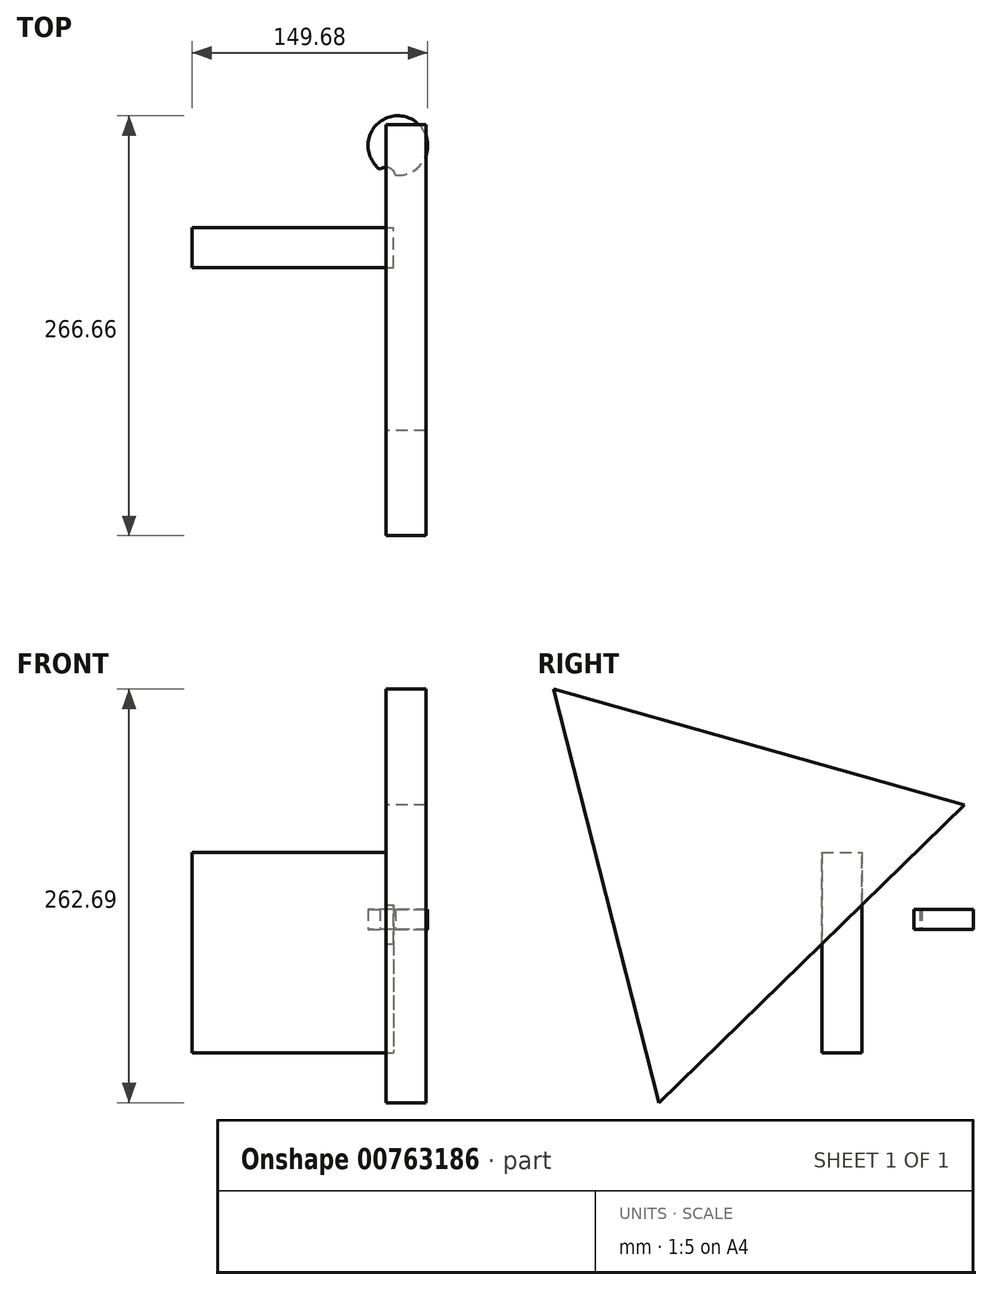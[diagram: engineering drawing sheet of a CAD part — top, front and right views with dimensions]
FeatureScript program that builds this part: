
annotation { "Feature Type Name" : "Feature", "Feature Type Description" : "" }
export const myFeature = defineFeature(function(context is Context, id is Id, definition is map)
    precondition{}
    {
        {
            var Q0;
            Q0=qCreatedBy(makeId("Front.planeOp"),FACE);
            var sketch = newSketch(context, id + "F0", { "sketchPlane" : qUnion([Q0])});
            skLineSegment(sketch, "E0.bottom", {"start": v(-123.14, 48.88) * mm, "end": v(4.73, 48.88) * mm});
            skLineSegment(sketch, "E0.top", {"start": v(-123.14, -78.51) * mm, "end": v(4.73, -78.51) * mm});
            skLineSegment(sketch, "E0.left", {"start": v(-123.14, 48.88) * mm, "end": v(-123.14, -78.51) * mm});
            skLineSegment(sketch, "E0.right", {"start": v(4.73, 48.88) * mm, "end": v(4.73, -78.51) * mm});
            skSolve(sketch);
        }
        {
            var Q0;
            Q0=makeQuery(id+"F0.imprint","IMPRINT",FACE,{"disambiguationData":[TD([[makeQuery(id+"F0.imprint","IMPRINT",EDGE,{"derivedFrom":sQuery(id+"F0.wireOp",EDGE,"E0.bottom")}),-1.0]])]});
            extrude(context, id + "F1", {"entities" : qUnion([Q0]), "depth" : 25.4 * mm, "offsetDistance" : 25.4 * mm});
        }
        {
            var Q0;
            Q0=qCreatedBy(makeId("Top.planeOp"),FACE);
            var sketch = newSketch(context, id + "F2", { "sketchPlane" : qUnion([Q0])});
            skCircle(sketch, "E1", {"center": v(0, 32.06) * mm, "radius": 6.2 * mm});
            skCircle(sketch, "E2", {"center": v(30.49, 19.7) * mm, "radius": 19.19 * mm});
            skCircle(sketch, "E3", {"center": v(41.85, 20.66) * mm, "radius": 26.39 * mm});
            skCircle(sketch, "E4", {"center": v(61.9, 3.51) * mm, "radius": 31.8 * mm});
            skCircle(sketch, "E5", {"center": v(19.64, 0) * mm, "radius": 21.64 * mm});
            skCircle(sketch, "E6", {"center": v(7.61, 52.04) * mm, "radius": 18.93 * mm});
            skSolve(sketch);
        }
        {
            var Q0;
            {var subQ0=sQuery(id+"F2.wireOp",EDGE,"E6");var subQ1=sQuery(id+"F2.wireOp",EDGE,"E1");var subQ2=makeQuery(id+"F2.imprint","INTERSECT",VERTEX,{"disambiguationData":[OD(0.0)],"derivedFrom":[subQ1,subQ0]});Q0=makeQuery(id+"F2.imprint","IMPRINT",FACE,{"disambiguationData":[TD([[makeQuery(id+"F2.imprint","IMPRINT",EDGE,{"disambiguationData":[TD([[subQ2,1.0]])],"derivedFrom":subQ1}),-1.0]])]});}
            extrude(context, id + "F3", {"entities" : qUnion([Q0]), "depth" : 12.7 * mm, "offsetDistance" : 25.4 * mm});
        }
        {
            var Q0;
            Q0=qCreatedBy(makeId("Right.planeOp"),FACE);
            var sketch = newSketch(context, id + "F4", { "sketchPlane" : qUnion([Q0])});
            skCircle(sketch, "E7.cCircle", {"center": v(-86.47, 40.43) * mm, "radius": 78.24 * mm, "construction": true});
            skLineSegment(sketch, "E7.0", {"start": v(65.2, 78.99) * mm, "end": v(-128.9, -110.2) * mm});
            skLineSegment(sketch, "E7.1", {"start": v(-128.9, -110.2) * mm, "end": v(-195.7, 152.5) * mm});
            skLineSegment(sketch, "E7.2", {"start": v(-195.7, 152.5) * mm, "end": v(65.2, 78.99) * mm});
            skPoint(sketch, "E7.0.midPoint", {"position": v(-31.86, -15.6) * mm});
            skSolve(sketch);
        }
        {
            var Q0;
            Q0=makeQuery(id+"F4.imprint","IMPRINT",FACE,{"disambiguationData":[TD([[makeQuery(id+"F4.imprint","IMPRINT",EDGE,{"derivedFrom":sQuery(id+"F4.wireOp",EDGE,"E7.0")}),-1.0]])]});
            extrude(context, id + "F5", {"entities" : qUnion([Q0]), "operationType" : NewBodyOperationType.ADD, "depth" : 25.4 * mm, "offsetDistance" : 25.4 * mm});
        }
    });
